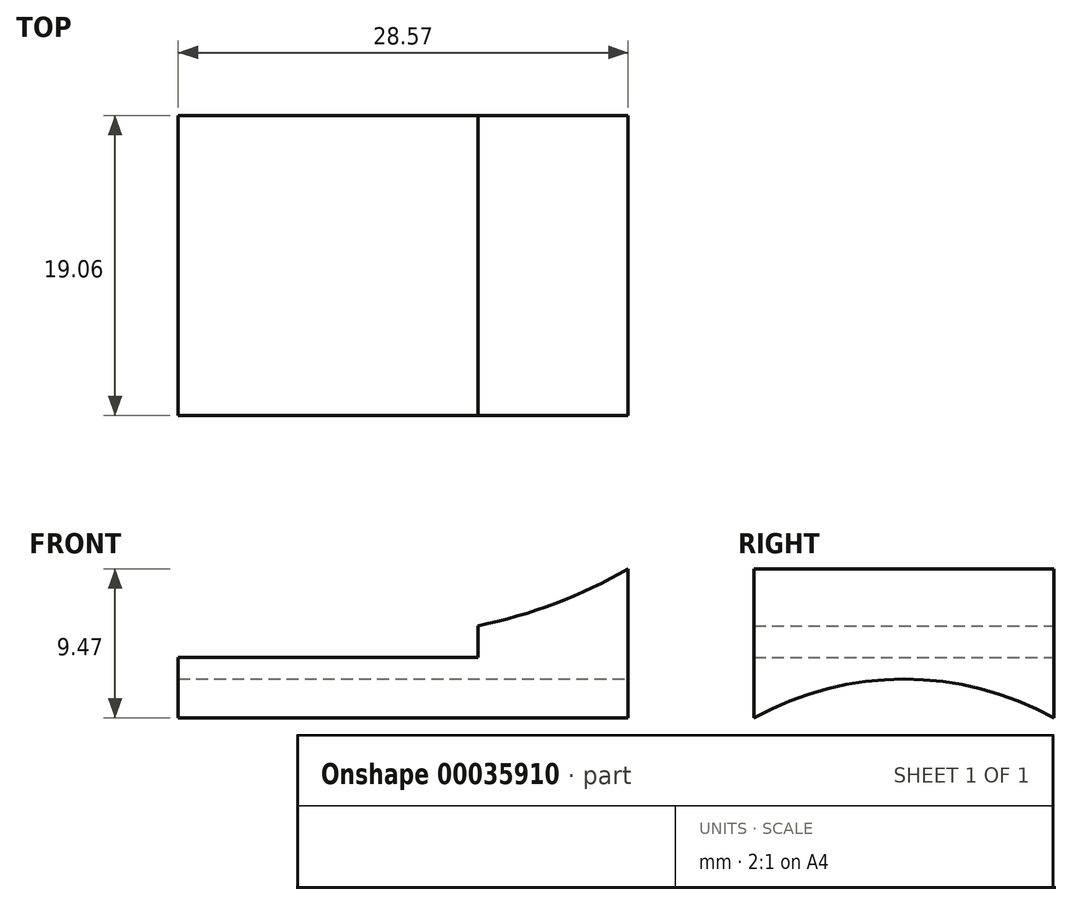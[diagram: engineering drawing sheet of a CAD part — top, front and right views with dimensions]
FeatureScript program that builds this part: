
annotation { "Feature Type Name" : "Feature", "Feature Type Description" : "" }
export const myFeature = defineFeature(function(context is Context, id is Id, definition is map)
    precondition{}
    {
        {
            var Q0;
            Q0=qCreatedBy(makeId("Front.planeOp"),FACE);
            var sketch = newSketch(context, id + "F0", { "sketchPlane" : qUnion([Q0])});
            skLineSegment(sketch, "E0", {"start": v(0, 0) * mm, "end": v(-28.58, 0) * mm});
            skLineSegment(sketch, "E1", {"start": v(-28.58, 0) * mm, "end": v(-28.58, 3.86) * mm});
            skLineSegment(sketch, "E2", {"start": v(-28.58, 3.86) * mm, "end": v(-9.53, 3.86) * mm});
            skLineSegment(sketch, "E3", {"start": v(-9.53, 3.86) * mm, "end": v(-9.53, 5.86) * mm});
            skLineSegment(sketch, "E4", {"start": v(0, 0) * mm, "end": v(0, 9.47) * mm});
            skArc(sketch, "E5", {"start": v(-9.52, 5.86) * mm, "mid": v(-4.62, 7.28) * mm, "end": v(0, 9.47) * mm});
            skSolve(sketch);
        }
        {
            var Q0;
            Q0=makeQuery(id+"F0.imprint","IMPRINT",FACE,{"disambiguationData":[TD([[makeQuery(id+"F0.imprint","IMPRINT",EDGE,{"derivedFrom":sQuery(id+"F0.wireOp",EDGE,"E0")}),-1.0]])]});
            extrude(context, id + "F1", {"entities" : qUnion([Q0]), "depth" : 19.05 * mm, "symmetric" : true});
        }
        {
            var Q0;
            Q0=makeQuery(id+"F1.opExtrude","SWEPT_FACE",FACE,{"disambiguationData":[OSD([sQuery(id+"F0.wireOp",EDGE,"E4")])]});
            var sketch = newSketch(context, id + "F2", { "sketchPlane" : qUnion([Q0])});
            skLineSegment(sketch, "E6.0", {"start": v(-9.53, 0) * mm, "end": v(9.52, 0) * mm});
            skArc(sketch, "E7", {"start": v(9.52, 0) * mm, "mid": v(0, 2.48) * mm, "end": v(-9.52, 0) * mm});
            skSolve(sketch);
        }
        {
            var Q0;
            Q0=makeQuery(id+"F2.imprint","IMPRINT",FACE,{"disambiguationData":[TD([[makeQuery(id+"F2.imprint","IMPRINT",EDGE,{"derivedFrom":sQuery(id+"F2.wireOp",EDGE,"E6.0")}),1.0]])]});
            extrude(context, id + "F3", {"entities" : qUnion([Q0]), "operationType" : NewBodyOperationType.REMOVE, "endBound" : BoundingType.THROUGH_ALL, "oppositeDirection" : true, "depth" : 25.4 * mm});
        }
    });
